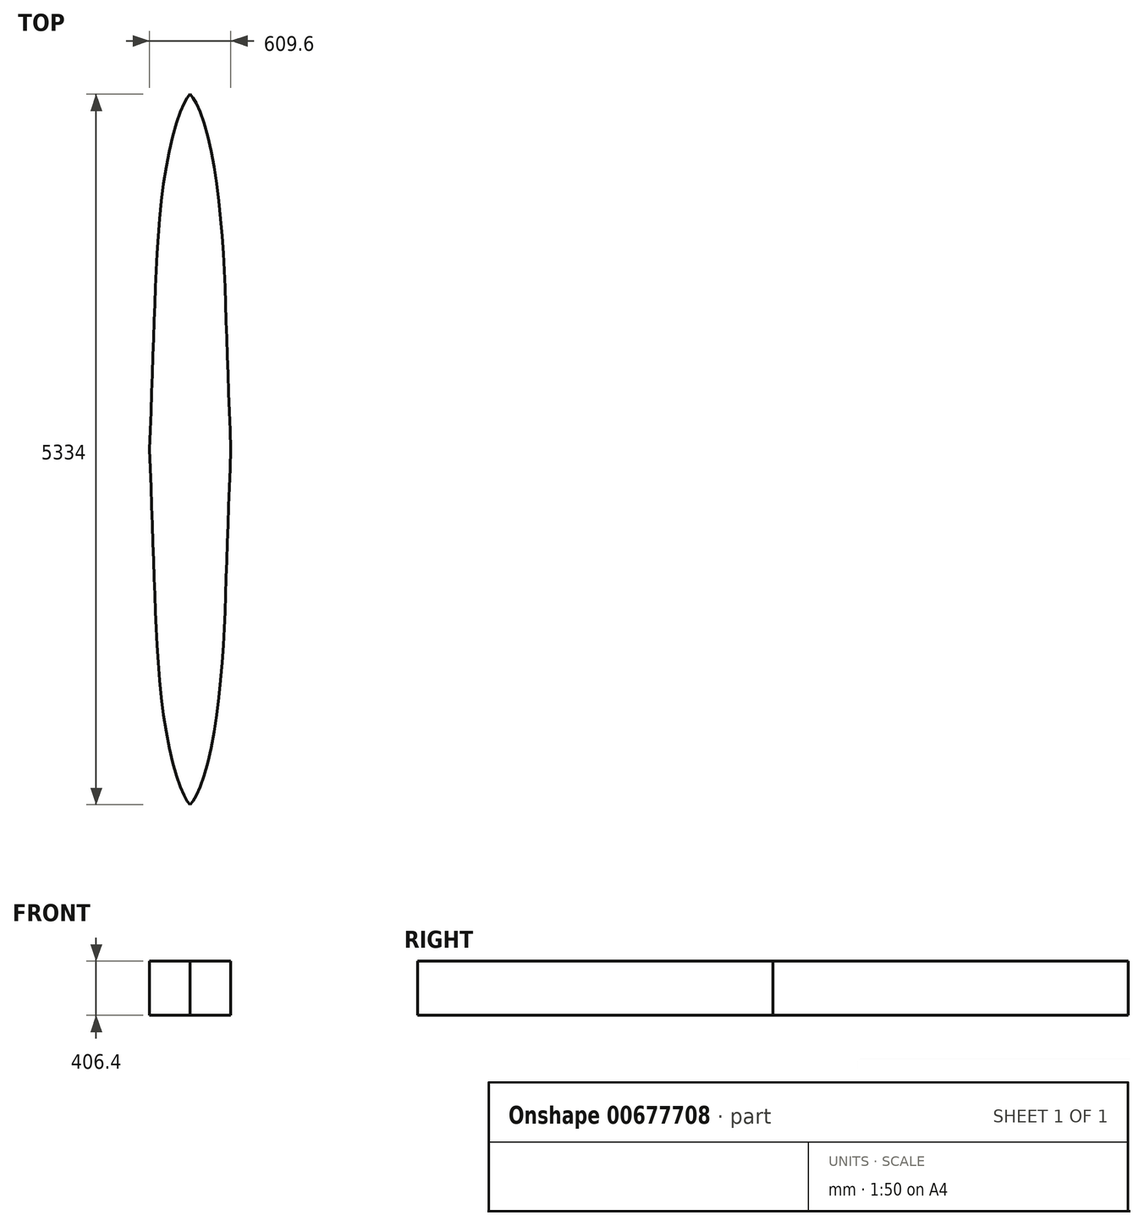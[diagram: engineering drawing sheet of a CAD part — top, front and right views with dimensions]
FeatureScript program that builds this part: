
annotation { "Feature Type Name" : "Feature", "Feature Type Description" : "" }
export const myFeature = defineFeature(function(context is Context, id is Id, definition is map)
    precondition{}
    {
        {
            var Q0;
            Q0=qCreatedBy(makeId("Top.planeOp"),FACE);
            var sketch = newSketch(context, id + "F0", { "sketchPlane" : qUnion([Q0])});
            skFitSpline(sketch, "E0", {"points": [v(-3593.69, 0) * mm, v(-3634.27, -57.36) * mm, v(-3743.15, -387.9) * mm, v(-3836.47, -1107.28) * mm, v(-3867.58, -1818.9) * mm, v(-3898.49, -2667) * mm], "startDerivative": vector(-505.91, -588.38) * mm, "endDerivative": vector(-125.18, -3285.52) * mm});
            skFitSpline(sketch, "E1.MirrorCS", {"points": [v(-3593.69, 0) * mm, v(-3553.11, -57.36) * mm, v(-3444.23, -387.9) * mm, v(-3350.9, -1107.28) * mm, v(-3319.8, -1818.9) * mm, v(-3288.89, -2667) * mm], "startDerivative": vector(505.91, -588.38) * mm, "endDerivative": vector(125.18, -3285.52) * mm});
            skFitSpline(sketch, "E2.MirrorCS", {"points": [v(-3593.69, -5334) * mm, v(-3634.27, -5276.64) * mm, v(-3743.15, -4946.1) * mm, v(-3836.47, -4226.72) * mm, v(-3867.58, -3515.1) * mm, v(-3898.49, -2667) * mm], "startDerivative": vector(-505.91, 588.38) * mm, "endDerivative": vector(-125.18, 3285.52) * mm});
            skFitSpline(sketch, "E3.MirrorCS", {"points": [v(-3593.69, -5334) * mm, v(-3553.11, -5276.64) * mm, v(-3444.23, -4946.1) * mm, v(-3350.9, -4226.72) * mm, v(-3319.8, -3515.1) * mm, v(-3288.89, -2667) * mm], "startDerivative": vector(505.91, 588.38) * mm, "endDerivative": vector(125.18, 3285.52) * mm});
            skSolve(sketch);
        }
        {
            var Q0;
            Q0 = qSketchRegion(id + "F0", true);
            extrude(context, id + "F1", {"entities" : qUnion([Q0]), "depth" : 406.4 * mm, "offsetDistance" : 25.4 * mm});
        }
    });
